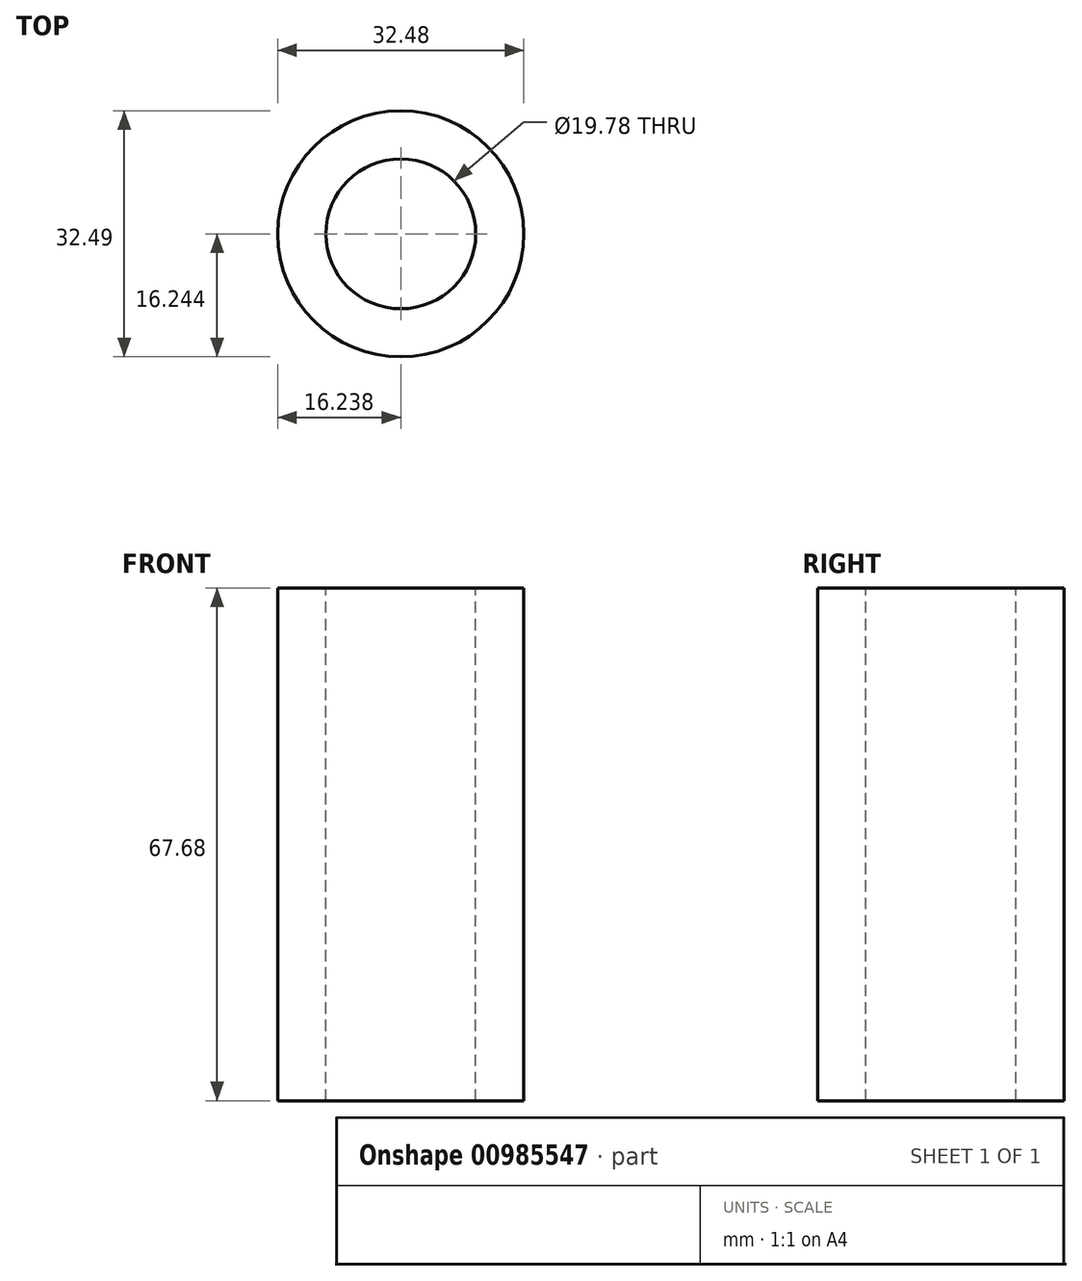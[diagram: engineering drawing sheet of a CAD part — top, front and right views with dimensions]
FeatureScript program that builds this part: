
annotation { "Feature Type Name" : "Feature", "Feature Type Description" : "" }
export const myFeature = defineFeature(function(context is Context, id is Id, definition is map)
    precondition{}
    {
        {
            var Q0;
            Q0=qCreatedBy(makeId("Top.planeOp"),FACE);
            var sketch = newSketch(context, id + "F0", { "sketchPlane" : qUnion([Q0])});
            skCircle(sketch, "E0", {"center": v(-20.2, 35.68) * mm, "radius": 15.97 * mm});
            skCircle(sketch, "E1", {"center": v(-20.2, 35.68) * mm, "radius": 16.24 * mm});
            skSolve(sketch);
        }
        {
            var Q0;
            Q0 = qSketchRegion(id + "F0", true);
            var Q1;
            Q1=makeQuery(id+"F0.imprint","IMPRINT",FACE,{"disambiguationData":[TD([[makeQuery(id+"F0.imprint","IMPRINT",EDGE,{"derivedFrom":sQuery(id+"F0.wireOp",EDGE,"E0")}),1.0]])]});
            extrude(context, id + "F1", {"entities" : qUnion([Q0, Q1]), "depth" : 67.68 * mm, "offsetDistance" : 25.4 * mm});
        }
        {
            var Q0;
            Q0=makeQuery(id+"F1.opExtrude","CAP_FACE",FACE,{"disambiguationData":[OSD([sQuery(id+"F0.wireOp",EDGE,"E1")])],"isStart":false});
            var sketch = newSketch(context, id + "F2", { "sketchPlane" : qUnion([Q0])});
            skCircle(sketch, "E2.0", {"center": v(-20.2, 35.68) * mm, "radius": 9.9 * mm});
            skSolve(sketch);
        }
        {
            var Q0;
            Q0=makeQuery(id+"F2.imprint","IMPRINT",FACE,{"disambiguationData":[TD([[makeQuery(id+"F2.imprint","IMPRINT",EDGE,{"derivedFrom":sQuery(id+"F2.wireOp",EDGE,"E2.0")}),1.0]])]});
            var Q1;
            Q1=makeQuery(id+"F1.opExtrude","CAP_FACE",FACE,{"disambiguationData":[OSD([sQuery(id+"F0.wireOp",EDGE,"E1")])],"isStart":true});
            extrude(context, id + "F3", {"entities" : qUnion([Q0, Q1]), "operationType" : NewBodyOperationType.REMOVE, "endBound" : BoundingType.THROUGH_ALL, "oppositeDirection" : true, "depth" : 25.4 * mm, "offsetDistance" : 25.4 * mm});
        }
    });
